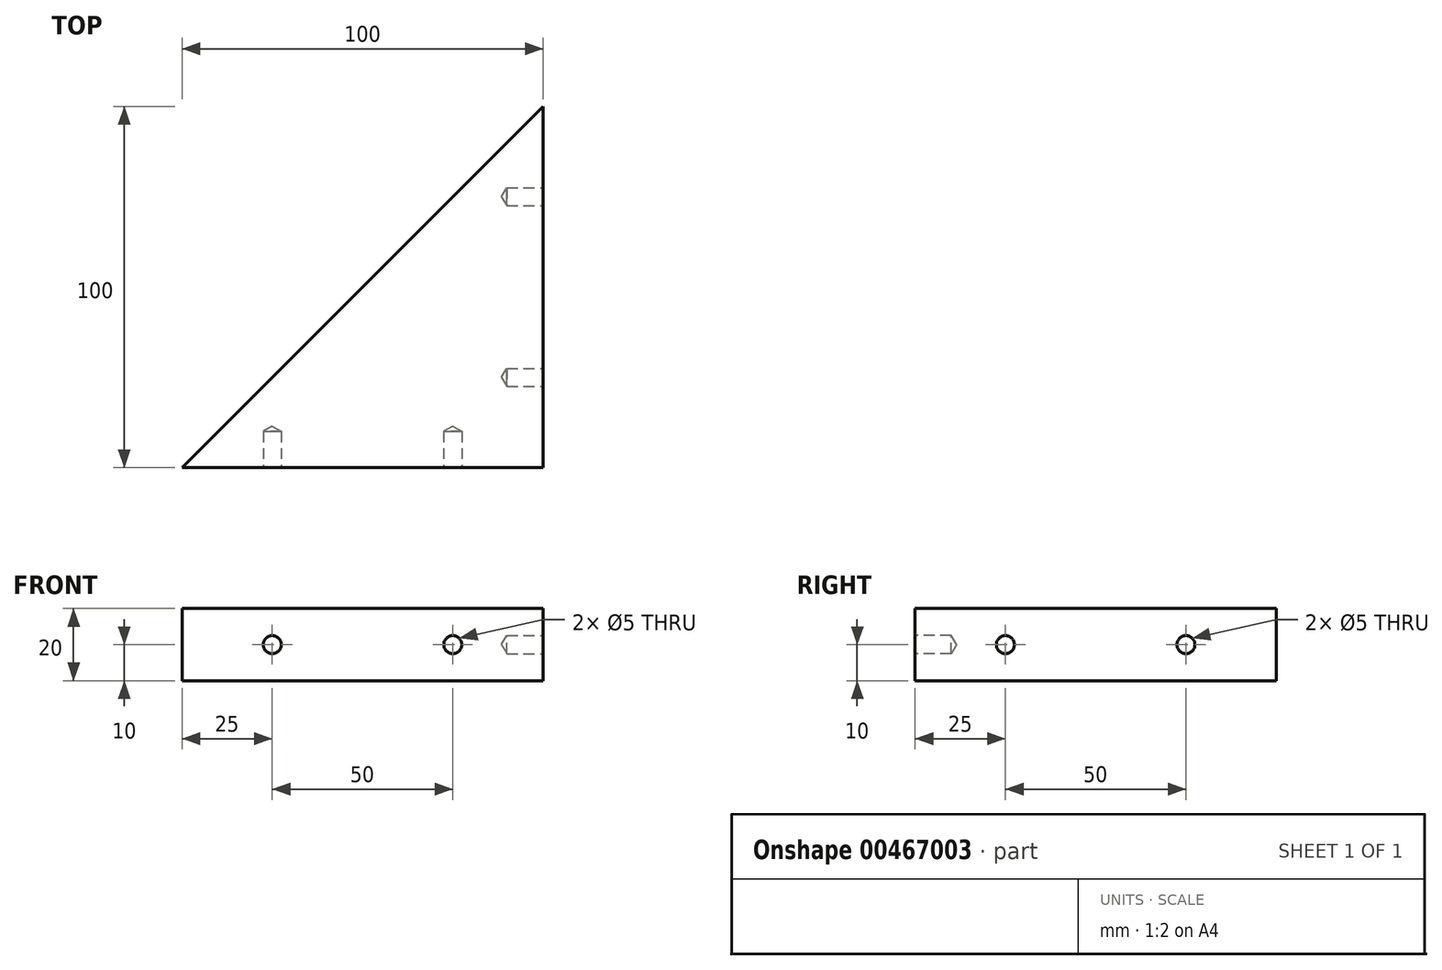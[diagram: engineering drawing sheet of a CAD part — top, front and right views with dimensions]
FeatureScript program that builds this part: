
annotation { "Feature Type Name" : "Feature", "Feature Type Description" : "" }
export const myFeature = defineFeature(function(context is Context, id is Id, definition is map)
    precondition{}
    {
        {
            var Q0;
            Q0=qCreatedBy(makeId("Top.planeOp"),FACE);
            var sketch = newSketch(context, id + "F0", { "sketchPlane" : qUnion([Q0])});
            skLineSegment(sketch, "E0.bottom", {"start": v(0, 0) * mm, "end": v(-100, 0) * mm});
            skLineSegment(sketch, "E0.top", {"start": v(0, 100) * mm, "end": v(-100, 100) * mm});
            skLineSegment(sketch, "E0.left", {"start": v(0, 0) * mm, "end": v(0, 100) * mm});
            skLineSegment(sketch, "E0.right", {"start": v(-100, 0) * mm, "end": v(-100, 100) * mm});
            skLineSegment(sketch, "E1", {"start": v(-100, 0) * mm, "end": v(0, 100) * mm});
            skSolve(sketch);
        }
        {
            var Q0;
            Q0=makeQuery(id+"F0.imprint","IMPRINT",FACE,{"disambiguationData":[TD([[makeQuery(id+"F0.imprint","IMPRINT",EDGE,{"derivedFrom":sQuery(id+"F0.wireOp",EDGE,"E0.bottom")}),-1.0]])]});
            extrude(context, id + "F1", {"entities" : qUnion([Q0]), "depth" : 20 * mm});
        }
        {
            var Q0;
            Q0=makeQuery(id+"F1.opExtrude","SWEPT_FACE",FACE,{"disambiguationData":[OSD([sQuery(id+"F0.wireOp",EDGE,"E0.left")])]});
            var sketch = newSketch(context, id + "F2", { "sketchPlane" : qUnion([Q0])});
            skLineSegment(sketch, "E2", {"start": v(50, 0) * mm, "end": v(50, 20) * mm});
            skLineSegment(sketch, "E3.bottom", {"start": v(100, 20) * mm, "end": v(50, 20) * mm});
            skLineSegment(sketch, "E3.top", {"start": v(100, 0) * mm, "end": v(50, 0) * mm});
            skLineSegment(sketch, "E3.left", {"start": v(100, 20) * mm, "end": v(100, 0) * mm});
            skLineSegment(sketch, "E3.right", {"start": v(50, 20) * mm, "end": v(50, 0) * mm});
            skLineSegment(sketch, "E4.bottom", {"start": v(50, 0) * mm, "end": v(0, 0) * mm});
            skLineSegment(sketch, "E4.top", {"start": v(50, 20) * mm, "end": v(0, 20) * mm});
            skLineSegment(sketch, "E4.right", {"start": v(0, 0) * mm, "end": v(0, 20) * mm});
            skPoint(sketch, "E5", {"position": v(75, 10) * mm});
            skPoint(sketch, "E5.positionSnap0", {"position": v(100, 10) * mm});
            skPoint(sketch, "E5.positionSnap1", {"position": v(75, 20) * mm});
            skPoint(sketch, "E6", {"position": v(25, 10) * mm});
            skPoint(sketch, "E6.positionSnap0", {"position": v(25, 20) * mm});
            skPoint(sketch, "E6.positionSnap1", {"position": v(50, 10) * mm});
            skSolve(sketch);
        }
        {
            var Q0;
            Q0=sQuery(id+"F2.wireOp",VERTEX,"E5");
            var Q1;
            Q1=sQuery(id+"F2.wireOp",VERTEX,"E6");
            var Q2;
            Q2=makeQuery(id+"F1.opExtrude","SWEPT_BODY",BODY,{"disambiguationData":[OSD([sQuery(id+"F0.wireOp",EDGE,"E0.bottom"),sQuery(id+"F0.wireOp",EDGE,"E0.left"),sQuery(id+"F0.wireOp",EDGE,"E1")])]});
            hole(context, id + "F3", {"style" : HoleStyle.SIMPLE, "endStyle" : HoleEndStyle.BLIND, "holeDiameter" : 5 * mm, "holeDepth" : 10 * mm, "isTappedThrough" : true, "tappedDepth" : 12 * mm, "tapClearance" : 3, "locations" : qUnion([Q0, Q1]), "scope" : qUnion([Q2])});
        }
        {
            var Q0;
            Q0=makeQuery(id+"F1.opExtrude","SWEPT_FACE",FACE,{"disambiguationData":[OSD([sQuery(id+"F0.wireOp",EDGE,"E0.bottom")])]});
            var sketch = newSketch(context, id + "F4", { "sketchPlane" : qUnion([Q0])});
            skLineSegment(sketch, "E7.bottom", {"start": v(0, 20) * mm, "end": v(-50, 20) * mm});
            skLineSegment(sketch, "E7.top", {"start": v(0, 0) * mm, "end": v(-50, 0) * mm});
            skLineSegment(sketch, "E7.left", {"start": v(0, 20) * mm, "end": v(0, 0) * mm});
            skLineSegment(sketch, "E7.right", {"start": v(-50, 20) * mm, "end": v(-50, 0) * mm});
            skLineSegment(sketch, "E8.bottom", {"start": v(-50, 0) * mm, "end": v(-100, 0) * mm});
            skLineSegment(sketch, "E8.top", {"start": v(-50, 20) * mm, "end": v(-100, 20) * mm});
            skLineSegment(sketch, "E8.left", {"start": v(-50, 0) * mm, "end": v(-50, 20) * mm});
            skLineSegment(sketch, "E8.right", {"start": v(-100, 0) * mm, "end": v(-100, 20) * mm});
            skPoint(sketch, "E9", {"position": v(-75, 10) * mm});
            skPoint(sketch, "E9.positionSnap0", {"position": v(-75, 20) * mm});
            skPoint(sketch, "E9.positionSnap1", {"position": v(-50, 10) * mm});
            skPoint(sketch, "E10", {"position": v(-25, 10) * mm});
            skPoint(sketch, "E10.positionSnap0", {"position": v(-25, 20) * mm});
            skSolve(sketch);
        }
        {
            var Q0;
            Q0=sQuery(id+"F4.wireOp",VERTEX,"E10");
            var Q1;
            Q1=sQuery(id+"F4.wireOp",VERTEX,"E9");
            var Q2;
            Q2=makeQuery(id+"F1.opExtrude","SWEPT_BODY",BODY,{"disambiguationData":[OSD([sQuery(id+"F0.wireOp",EDGE,"E0.bottom"),sQuery(id+"F0.wireOp",EDGE,"E0.left"),sQuery(id+"F0.wireOp",EDGE,"E1")])]});
            hole(context, id + "F5", {"style" : HoleStyle.SIMPLE, "endStyle" : HoleEndStyle.BLIND, "holeDiameter" : 5 * mm, "holeDepth" : 10 * mm, "isTappedThrough" : true, "tappedDepth" : 12 * mm, "tapClearance" : 3, "locations" : qUnion([Q0, Q1]), "scope" : qUnion([Q2])});
        }
    });
